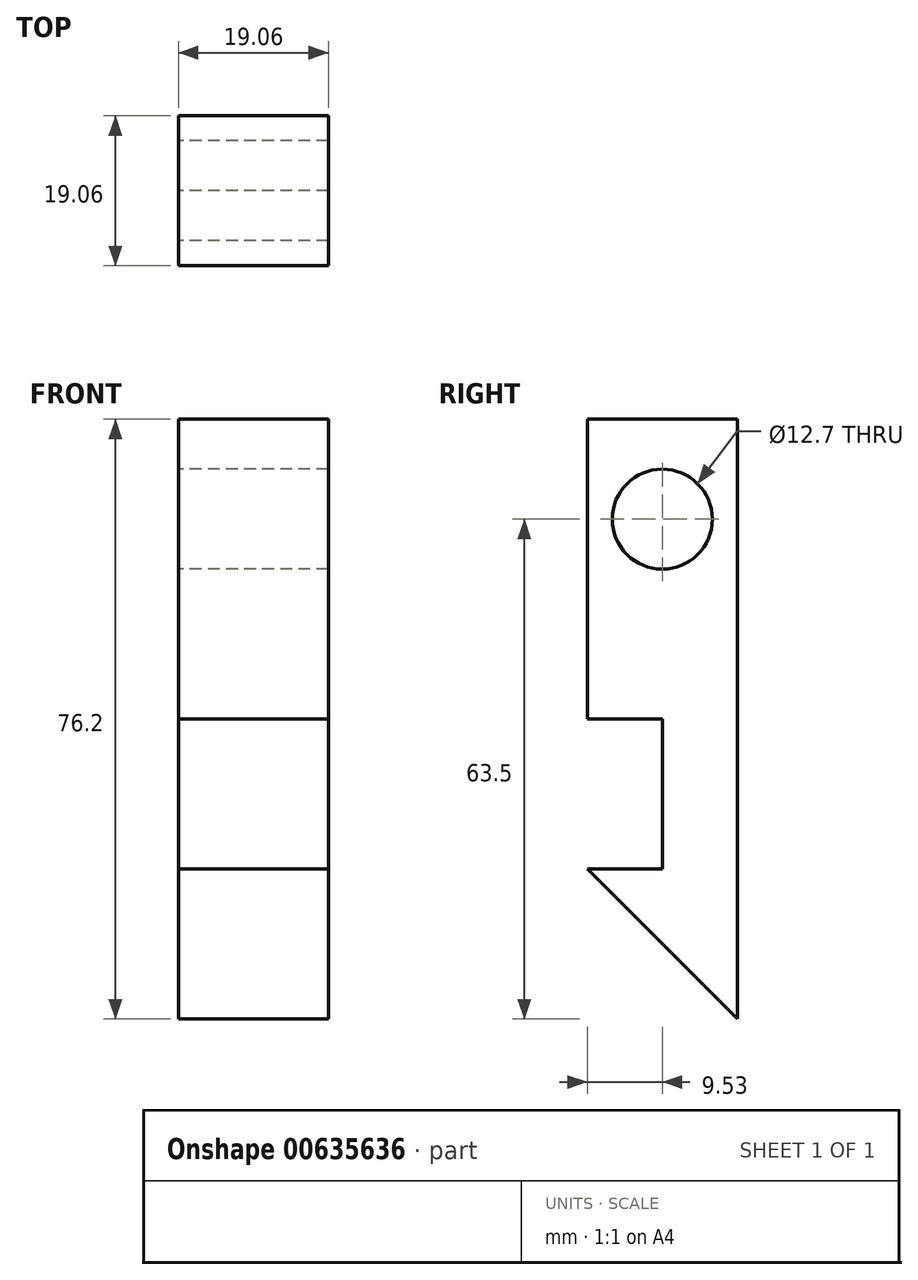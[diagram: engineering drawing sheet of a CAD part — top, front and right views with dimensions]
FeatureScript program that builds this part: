
annotation { "Feature Type Name" : "Feature", "Feature Type Description" : "" }
export const myFeature = defineFeature(function(context is Context, id is Id, definition is map)
    precondition{}
    {
        {
            var Q0;
            Q0=qCreatedBy(makeId("Right.planeOp"),FACE);
            var sketch = newSketch(context, id + "F0", { "sketchPlane" : qUnion([Q0])});
            skLineSegment(sketch, "E0.bottom", {"start": v(-9.53, 38.1) * mm, "end": v(9.52, 38.1) * mm});
            skLineSegment(sketch, "E0.left", {"start": v(-9.53, 38.1) * mm, "end": v(-9.53, 0) * mm});
            skLineSegment(sketch, "E0.right", {"start": v(9.52, 38.1) * mm, "end": v(9.52, -38.1) * mm});
            skPoint(sketch, "E0.middle", {"position": v(0, 0) * mm});
            skLineSegment(sketch, "E1", {"start": v(9.52, -38.1) * mm, "end": v(-9.53, -19.05) * mm});
            skPoint(sketch, "E0.top.start.orphan", {"position": v(-9.53, -38.1) * mm});
            skLineSegment(sketch, "E2.bottom", {"start": v(-9.53, -19.05) * mm, "end": v(0, -19.05) * mm});
            skLineSegment(sketch, "E2.top", {"start": v(-9.53, 0) * mm, "end": v(0, 0) * mm});
            skLineSegment(sketch, "E2.right", {"start": v(0, -19.05) * mm, "end": v(0, 0) * mm});
            skCircle(sketch, "E3", {"center": v(0, 25.4) * mm, "radius": 6.35 * mm});
            skPoint(sketch, "E3.centerSnap0", {"position": v(0, 38.1) * mm});
            skSolve(sketch);
        }
        {
            var Q0;
            Q0 = qSketchRegion(id + "F0", true);
            extrude(context, id + "F1", {"entities" : qUnion([Q0]), "endBound" : BoundingType.SYMMETRIC, "depth" : 19.05 * mm, "offsetDistance" : 25.4 * mm});
        }
    });
